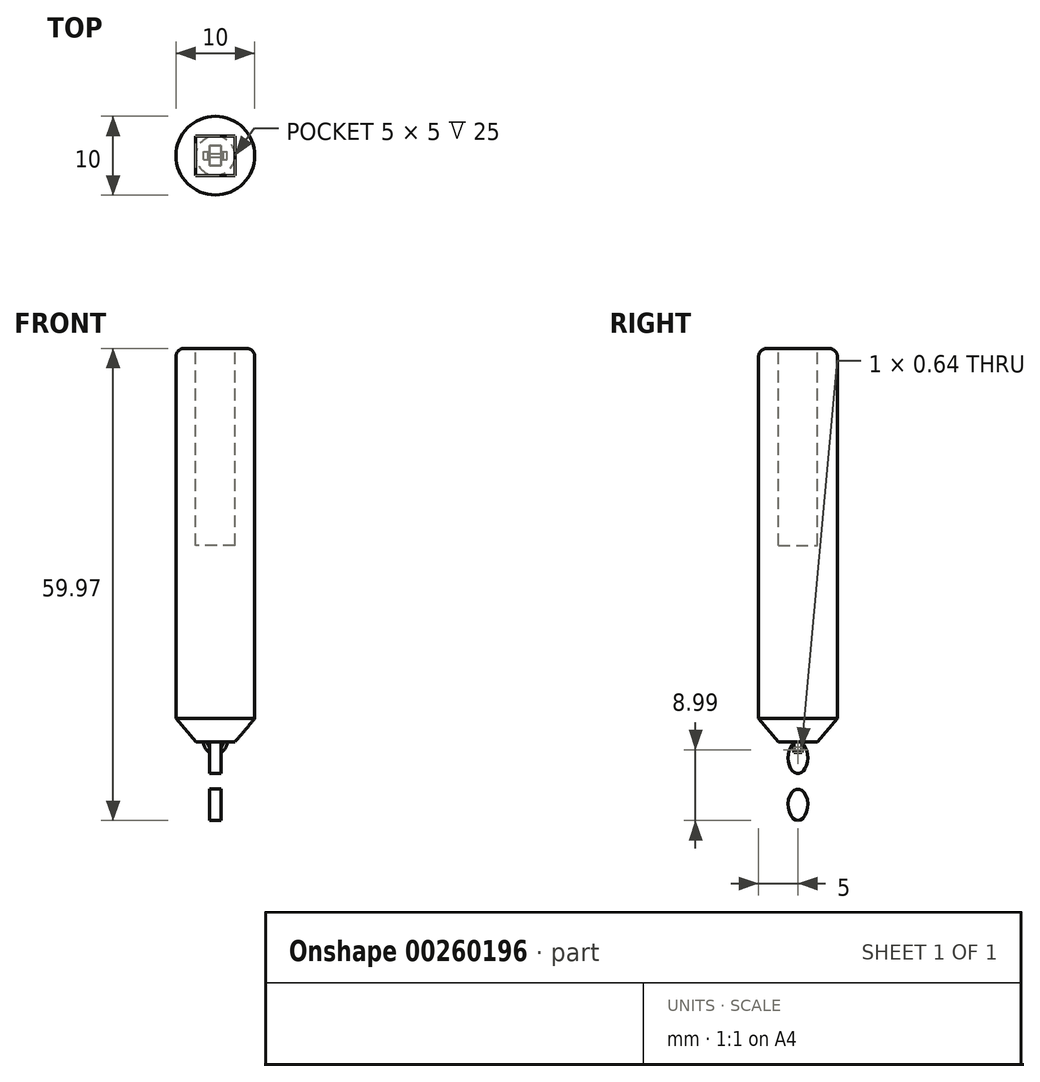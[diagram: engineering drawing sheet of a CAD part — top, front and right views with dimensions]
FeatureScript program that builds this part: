
annotation { "Feature Type Name" : "Feature", "Feature Type Description" : "" }
export const myFeature = defineFeature(function(context is Context, id is Id, definition is map)
    precondition{}
    {
        {
            var Q0;
            Q0=qCreatedBy(makeId("Top.planeOp"),FACE);
            var sketch = newSketch(context, id + "F0", { "sketchPlane" : qUnion([Q0])});
            skCircle(sketch, "E0", {"center": v(0, 0) * mm, "radius": 5 * mm});
            skSolve(sketch);
        }
        {
            var Q0;
            Q0 = qSketchRegion(id + "F0", true);
            extrude(context, id + "F1", {"entities" : qUnion([Q0]), "depth" : 50 * mm});
        }
        {
            var Q0;
            Q0=makeQuery(id+"F1.opExtrude","CAP_FACE",FACE,{"disambiguationData":[OSD([sQuery(id+"F0.wireOp",EDGE,"E0")])],"isStart":false});
            var sketch = newSketch(context, id + "F2", { "sketchPlane" : qUnion([Q0])});
            skLineSegment(sketch, "E1.bottom", {"start": v(2.5, -2.5) * mm, "end": v(-2.5, -2.5) * mm});
            skLineSegment(sketch, "E1.top", {"start": v(2.5, 2.5) * mm, "end": v(-2.5, 2.5) * mm});
            skLineSegment(sketch, "E1.left", {"start": v(2.5, -2.5) * mm, "end": v(2.5, 2.5) * mm});
            skLineSegment(sketch, "E1.right", {"start": v(-2.5, -2.5) * mm, "end": v(-2.5, 2.5) * mm});
            skPoint(sketch, "E1.middle", {"position": v(0, 0) * mm});
            skSolve(sketch);
        }
        {
            var Q0;
            Q0 = qSketchRegion(id + "F2", true);
            extrude(context, id + "F3", {"entities" : qUnion([Q0]), "operationType" : NewBodyOperationType.REMOVE, "oppositeDirection" : true, "depth" : 25 * mm});
        }
        {
            var Q0;
            Q0=makeQuery(id+"F1.opExtrude","CAP_EDGE",EDGE,{"disambiguationData":[OSD([sQuery(id+"F0.wireOp",EDGE,"E0")])],"isStart":false});
            fillet(context, id + "F4", {"entities" : qUnion([Q0]), "radius" : 1 * mm, "tangentPropagation" : true, "allowEdgeOverflow" : false});
        }
        {
            var Q0;
            Q0=makeQuery(id+"F1.opExtrude","CAP_EDGE",EDGE,{"disambiguationData":[OSD([sQuery(id+"F0.wireOp",EDGE,"E0")])],"isStart":true});
            chamfer(context, id + "F5", {"entities" : qUnion([Q0]), "chamferType" : ChamferType.OFFSET_ANGLE, "width" : 3 * mm, "oppositeDirection" : false, "angle" : 40 * degree, "tangentPropagation" : true});
        }
        {
            var Q0;
            Q0=qCreatedBy(makeId("Front.planeOp"),FACE);
            var sketch = newSketch(context, id + "F6", { "sketchPlane" : qUnion([Q0])});
            skCircle(sketch, "E2", {"center": v(0, 0) * mm, "radius": 1.5 * mm});
            skSolve(sketch);
        }
        {
            var Q0;
            Q0 = qSketchRegion(id + "F6", true);
            extrude(context, id + "F7", {"entities" : qUnion([Q0]), "operationType" : NewBodyOperationType.ADD, "endBound" : BoundingType.SYMMETRIC, "depth" : 1 * mm});
        }
        {
            var Q0;
            Q0=makeQuery(id+"F7.opExtrude","CAP_FACE",FACE,{"disambiguationData":[OSD([sQuery(id+"F6.wireOp",EDGE,"E2")])],"isStart":false});
            var sketch = newSketch(context, id + "F8", { "sketchPlane" : qUnion([Q0])});
            skCircle(sketch, "E3", {"center": v(0, 0) * mm, "radius": 1 * mm});
            skSolve(sketch);
        }
        {
            var Q0;
            {var subQ0=sQuery(id+"F8.wireOp",EDGE,"E3");var subQ1=makeQuery(id+"F7.boolean.opBoolean","INTERSECT",EDGE,{"derivedFrom":[makeQuery(id+"F1.opExtrude","CAP_FACE",FACE,{"disambiguationData":[OSD([sQuery(id+"F0.wireOp",EDGE,"E0")])],"isStart":true}),makeQuery(id+"F7.opExtrude","CAP_FACE",FACE,{"disambiguationData":[OSD([sQuery(id+"F6.wireOp",EDGE,"E2")])],"isStart":false})]});var subQ2=makeQuery(id+"F8.imprint","INTERSECT",VERTEX,{"disambiguationData":[OD(0.0)],"derivedFrom":[subQ1,subQ0]});Q0=makeQuery(id+"F8.imprint","IMPRINT",FACE,{"disambiguationData":[TD([[makeQuery(id+"F8.imprint","IMPRINT",EDGE,{"disambiguationData":[TD([[subQ2,-1.0]])],"derivedFrom":subQ0}),1.0]])]});}
            extrude(context, id + "F9", {"entities" : qUnion([Q0]), "operationType" : NewBodyOperationType.REMOVE, "endBound" : BoundingType.SYMMETRIC, "oppositeDirection" : true, "depth" : 6 * mm});
        }
        {
            var Q0;
            Q0=qCreatedBy(makeId("Right.planeOp"),FACE);
            var sketch = newSketch(context, id + "F10", { "sketchPlane" : qUnion([Q0])});
            skEllipse(sketch, "E4", {"center": v(0, -1.97) * mm, "majorRadius": 2 * mm, "minorRadius": 1.25 * mm, "majorAxis": v(0, -1)});
            skFitSpline(sketch, "E5.0", {"points": [v(-0.16, -3.7) * mm, v(0, -3.72) * mm, v(0.16, -3.7) * mm, v(0.4, -3.58) * mm, v(0.68, -3.29) * mm, v(0.93, -2.7) * mm, v(1.02, -1.97) * mm, v(0.93, -1.25) * mm, v(0.68, -0.65) * mm, v(0.4, -0.36) * mm, v(0.16, -0.25) * mm, v(0, -0.22) * mm, v(-0.16, -0.25) * mm, v(-0.4, -0.36) * mm, v(-0.68, -0.65) * mm, v(-0.93, -1.25) * mm, v(-1.02, -1.97) * mm, v(-0.93, -2.7) * mm, v(-0.68, -3.29) * mm, v(-0.4, -3.58) * mm, v(-0.16, -3.7) * mm, v(0, -3.72) * mm, v(0.16, -3.7) * mm, v(-0.16, -3.7) * mm]});
            skEllipse(sketch, "E6.0.1.0", {"center": v(0, -7.97) * mm, "majorRadius": 2 * mm, "minorRadius": 1.25 * mm, "majorAxis": v(0, -1)});
            skEllipse(sketch, "E6.0.2.0", {"center": v(0, -13.97) * mm, "majorRadius": 2 * mm, "minorRadius": 1.25 * mm, "majorAxis": v(0, -1)});
            skEllipse(sketch, "E6.0.3.0", {"center": v(0, -19.97) * mm, "majorRadius": 2 * mm, "minorRadius": 1.25 * mm, "majorAxis": v(0, -1)});
            skEllipse(sketch, "E6.0.4.0", {"center": v(0, -25.97) * mm, "majorRadius": 2 * mm, "minorRadius": 1.25 * mm, "majorAxis": v(0, -1)});
            skEllipse(sketch, "E6.0.5.0", {"center": v(0, -31.97) * mm, "majorRadius": 2 * mm, "minorRadius": 1.25 * mm, "majorAxis": v(0, -1)});
            skEllipse(sketch, "E6.0.6.0", {"center": v(0, -37.97) * mm, "majorRadius": 2 * mm, "minorRadius": 1.25 * mm, "majorAxis": v(0, -1)});
            skLineSegment(sketch, "E6.direction1", {"start": v(0, -1.97) * mm, "end": v(25, -1.97) * mm, "construction": true});
            skLineSegment(sketch, "E6.direction2", {"start": v(0, -1.97) * mm, "end": v(0, -7.97) * mm, "construction": true});
            skFitSpline(sketch, "E7.0", {"points": [v(-0.16, -9.7) * mm, v(0, -9.72) * mm, v(0.16, -9.7) * mm, v(0.4, -9.58) * mm, v(0.68, -9.29) * mm, v(0.93, -8.7) * mm, v(1.02, -7.97) * mm, v(0.93, -7.25) * mm, v(0.68, -6.65) * mm, v(0.4, -6.36) * mm, v(0.16, -6.25) * mm, v(0, -6.22) * mm, v(-0.16, -6.25) * mm, v(-0.4, -6.36) * mm, v(-0.68, -6.65) * mm, v(-0.93, -7.25) * mm, v(-1.02, -7.97) * mm, v(-0.93, -8.7) * mm, v(-0.68, -9.29) * mm, v(-0.4, -9.58) * mm, v(-0.16, -9.7) * mm, v(0, -9.72) * mm, v(0.16, -9.7) * mm, v(-0.16, -9.7) * mm]});
            skFitSpline(sketch, "E8.0", {"points": [v(-0.33, -16.2) * mm, v(0, -16.25) * mm, v(0.33, -16.2) * mm, v(0.73, -16) * mm, v(1.13, -15.56) * mm, v(1.44, -14.82) * mm, v(1.55, -13.97) * mm, v(1.44, -13.12) * mm, v(1.13, -12.38) * mm, v(0.73, -11.94) * mm, v(0.33, -11.74) * mm, v(0, -11.7) * mm, v(-0.33, -11.74) * mm, v(-0.73, -11.94) * mm, v(-1.13, -12.38) * mm, v(-1.44, -13.12) * mm, v(-1.55, -13.97) * mm, v(-1.44, -14.82) * mm, v(-1.13, -15.56) * mm, v(-0.73, -16) * mm, v(-0.33, -16.2) * mm, v(0, -16.25) * mm, v(0.33, -16.2) * mm, v(-0.33, -16.2) * mm]});
            skFitSpline(sketch, "E9.0", {"points": [v(-0.33, -22.2) * mm, v(0, -22.25) * mm, v(0.33, -22.2) * mm, v(0.73, -22) * mm, v(1.13, -21.56) * mm, v(1.44, -20.82) * mm, v(1.55, -19.97) * mm, v(1.44, -19.12) * mm, v(1.13, -18.38) * mm, v(0.73, -17.94) * mm, v(0.33, -17.74) * mm, v(0, -17.7) * mm, v(-0.33, -17.74) * mm, v(-0.73, -17.94) * mm, v(-1.13, -18.38) * mm, v(-1.44, -19.12) * mm, v(-1.55, -19.97) * mm, v(-1.44, -20.82) * mm, v(-1.13, -21.56) * mm, v(-0.73, -22) * mm, v(-0.33, -22.2) * mm, v(0, -22.25) * mm, v(0.33, -22.2) * mm, v(-0.33, -22.2) * mm]});
            skFitSpline(sketch, "E10.0", {"points": [v(-0.33, -28.2) * mm, v(0, -28.25) * mm, v(0.33, -28.2) * mm, v(0.73, -28) * mm, v(1.13, -27.56) * mm, v(1.44, -26.82) * mm, v(1.55, -25.97) * mm, v(1.44, -25.12) * mm, v(1.13, -24.38) * mm, v(0.73, -23.94) * mm, v(0.33, -23.74) * mm, v(0, -23.7) * mm, v(-0.33, -23.74) * mm, v(-0.73, -23.94) * mm, v(-1.13, -24.38) * mm, v(-1.44, -25.12) * mm, v(-1.55, -25.97) * mm, v(-1.44, -26.82) * mm, v(-1.13, -27.56) * mm, v(-0.73, -28) * mm, v(-0.33, -28.2) * mm, v(0, -28.25) * mm, v(0.33, -28.2) * mm, v(-0.33, -28.2) * mm]});
            skFitSpline(sketch, "E11.0", {"points": [v(-0.33, -34.2) * mm, v(0, -34.25) * mm, v(0.33, -34.2) * mm, v(0.73, -34) * mm, v(1.13, -33.56) * mm, v(1.44, -32.82) * mm, v(1.55, -31.97) * mm, v(1.44, -31.12) * mm, v(1.13, -30.38) * mm, v(0.73, -29.94) * mm, v(0.33, -29.74) * mm, v(0, -29.7) * mm, v(-0.33, -29.74) * mm, v(-0.73, -29.94) * mm, v(-1.13, -30.38) * mm, v(-1.44, -31.12) * mm, v(-1.55, -31.97) * mm, v(-1.44, -32.82) * mm, v(-1.13, -33.56) * mm, v(-0.73, -34) * mm, v(-0.33, -34.2) * mm, v(0, -34.25) * mm, v(0.33, -34.2) * mm, v(-0.33, -34.2) * mm]});
            skFitSpline(sketch, "E12.0", {"points": [v(-0.33, -40.2) * mm, v(0, -40.25) * mm, v(0.33, -40.2) * mm, v(0.73, -40) * mm, v(1.13, -39.56) * mm, v(1.44, -38.82) * mm, v(1.55, -37.97) * mm, v(1.44, -37.12) * mm, v(1.13, -36.38) * mm, v(0.73, -35.94) * mm, v(0.33, -35.74) * mm, v(0, -35.7) * mm, v(-0.33, -35.74) * mm, v(-0.73, -35.94) * mm, v(-1.13, -36.38) * mm, v(-1.44, -37.12) * mm, v(-1.55, -37.97) * mm, v(-1.44, -38.82) * mm, v(-1.13, -39.56) * mm, v(-0.73, -40) * mm, v(-0.33, -40.2) * mm, v(0, -40.25) * mm, v(0.33, -40.2) * mm, v(-0.33, -40.2) * mm]});
            skSolve(sketch);
        }
        {
            var Q0;
            Q0=makeQuery(id+"F10.imprint","IMPRINT",FACE,{"disambiguationData":[TD([[makeQuery(id+"F10.imprint","IMPRINT",EDGE,{"derivedFrom":sQuery(id+"F10.wireOp",EDGE,"E4")}),1.0]])]});
            var Q1;
            Q1=makeQuery(id+"F10.imprint","IMPRINT",FACE,{"disambiguationData":[TD([[makeQuery(id+"F10.imprint","IMPRINT",EDGE,{"derivedFrom":sQuery(id+"F10.wireOp",EDGE,"E6.0.1.0")}),1.0]])]});
            var Q2;
            Q2=makeQuery(id+"F10.imprint","IMPRINT",FACE,{"disambiguationData":[TD([[makeQuery(id+"F10.imprint","IMPRINT",EDGE,{"derivedFrom":sQuery(id+"F10.wireOp",EDGE,"E6.0.6.0")}),-1.0]])]});
            var Q3;
            Q3=makeQuery(id+"F10.imprint","IMPRINT",FACE,{"disambiguationData":[TD([[makeQuery(id+"F10.imprint","IMPRINT",EDGE,{"derivedFrom":sQuery(id+"F10.wireOp",EDGE,"E6.0.5.0")}),-1.0]])]});
            var Q4;
            Q4=makeQuery(id+"F10.imprint","IMPRINT",FACE,{"disambiguationData":[TD([[makeQuery(id+"F10.imprint","IMPRINT",EDGE,{"derivedFrom":sQuery(id+"F10.wireOp",EDGE,"E6.0.4.0")}),-1.0]])]});
            var Q5;
            Q5=makeQuery(id+"F10.imprint","IMPRINT",FACE,{"disambiguationData":[TD([[makeQuery(id+"F10.imprint","IMPRINT",EDGE,{"derivedFrom":sQuery(id+"F10.wireOp",EDGE,"E6.0.3.0")}),-1.0]])]});
            var Q6;
            Q6=makeQuery(id+"F10.imprint","IMPRINT",FACE,{"disambiguationData":[TD([[makeQuery(id+"F10.imprint","IMPRINT",EDGE,{"derivedFrom":sQuery(id+"F10.wireOp",EDGE,"E6.0.2.0")}),-1.0]])]});
            var Q7;
            Q7=sQuery(id+"F10.wireOp",EDGE,"E4");
            var Q8;
            Q8=sQuery(id+"F10.wireOp",EDGE,"E5.0");
            extrude(context, id + "F11", {"entities" : qUnion([Q0, Q1, Q2, Q3, Q4, Q5, Q6]), "operationType" : NewBodyOperationType.ADD, "surfaceEntities" : qUnion([Q7, Q8]), "endBound" : BoundingType.SYMMETRIC, "depth" : 1.5 * mm});
        }
    });
